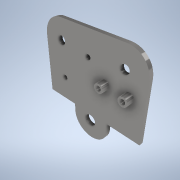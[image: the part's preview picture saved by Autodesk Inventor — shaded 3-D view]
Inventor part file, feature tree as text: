
AUTODESK INVENTOR PART (.ipt)
format: ipt  version: 2022 (Build 260153070, 153G)  size: 166,912 bytes
history: native  units: mm
features: extrude x3, sketch x1
ambient origin geometry x8: Origin, YZ Plane, XZ Plane, XY Plane, X Axis, Y Axis, Z Axis, Center Point
bodies: Solid1 (feature_tree)
feature tree (4):
  sketch  "Sketch1"  dims[d0=7.2mm d1=52.1mm d2=4.6mm d3=32.0mm d4=32.0mm d5=4.0mm d6=33.25mm d7=19.0mm d8=4.0mm d9=1.5mm d10=14.35mm d11=3.0mm d12=9.5mm d13=24.45mm d14=3.0mm d15=23.5mm d16=1.2mm d17=1.2mm d18=20.0mm d19=11.9mm d20=5.0mm d21=3.0mm d22=3.0mm d23=5.0mm d24=20.0mm d25=12.0mm d27=12.0mm d28=2.5mm d29=0.0mm d30=7.0mm d31=0.0mm d32=2.5mm d33=1.5mm d34=0.0mm d35=0.0mm]
  extrude  "Extrusion1"  Depth=1.5mm
  extrude  "Extrusion2"  Depth=1.5mm
  extrude  "Extrusion3"  Depth=1.5mm
